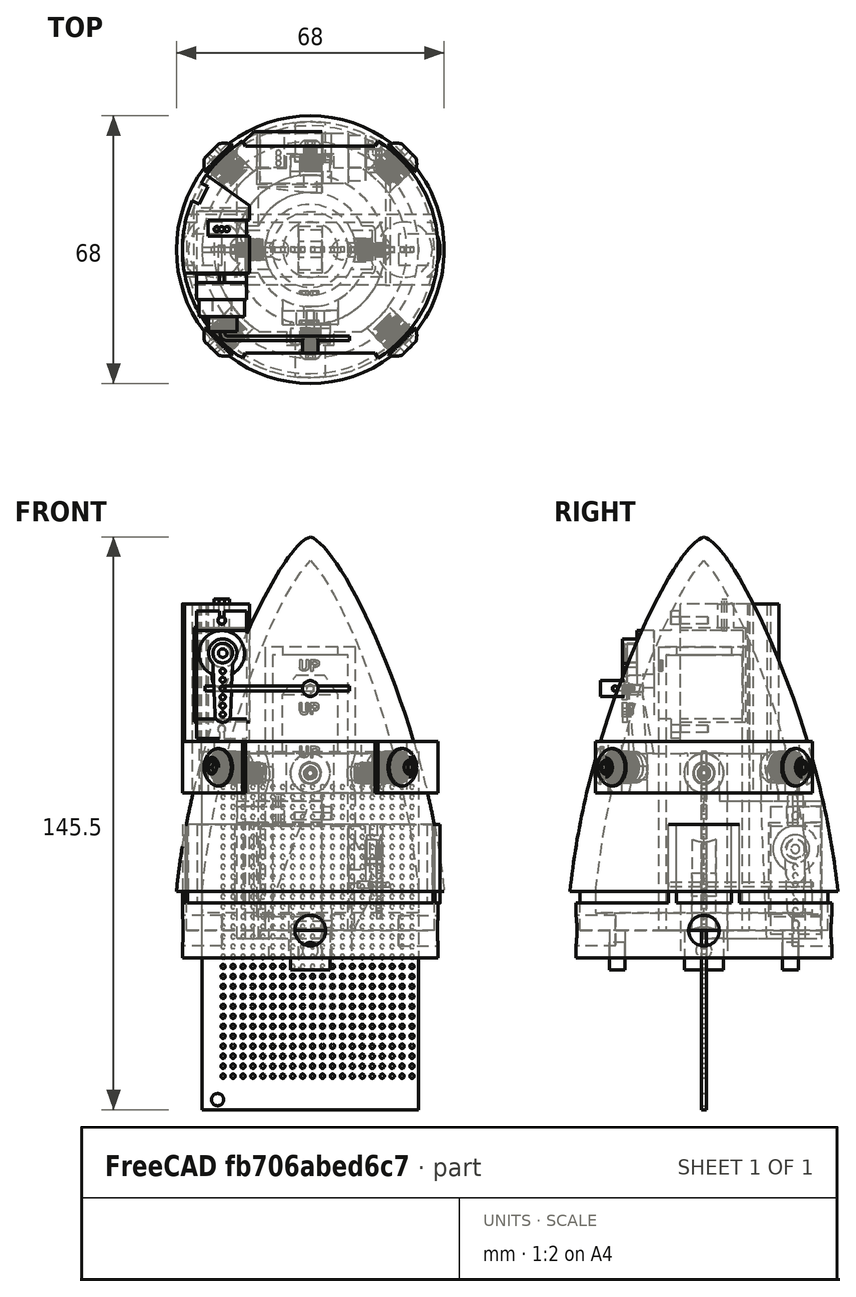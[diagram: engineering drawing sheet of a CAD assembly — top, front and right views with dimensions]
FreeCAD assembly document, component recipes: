
FREECAD ASSEMBLY — COMPONENT RECIPES ("slider")

This assembly document has 5 components, labeled P0..P4 below (a component is one placed body or linked part). 4 of them carry a construction recipe — the FreeCAD feature program that regenerates the part from scratch, quoted from this document or its linked companion documents; the rest are supplied as boundary geometry only. No exploded tour is included for this assembly.
COMPONENT P0 — recipe-attached ("66mm x 18" Body Tube", modeled in this document).
Construction recipe (the document's own serialized feature program — sketch geometry with constraints, then the solid features built on it; lengths are millimeters unless a unit is written):

FEATURE [Sketcher::SketchObject] Sketch006  label="Body Tube Sketch"
  FullyConstrained = true
  MapMode = 5
  Support = -> [XY_Plane004]
  sketch-geometry (2):
    g0: Circle CenterX=0 CenterY=0 CenterZ=0 NormalX=0 NormalY=0 NormalZ=1 AngleXU=0 Radius=33
    g1: Circle CenterX=0 CenterY=0 CenterZ=0 NormalX=0 NormalY=0 NormalZ=1 AngleXU=0 Radius=32.5
  constraints (4):
    c: Diameter(g0) = 66  'Outer Diameter'
    c: Diameter(g1) = 65  'Inner Diameter'
    c: Coincident(g1,g-1)  'Center1'
    c: Coincident(g1,g0)  'Center2'
FEATURE [PartDesign::Pad] Pad002  label="Body Tube Pad"
  AllowMultiFace = false
  Direction = (1,1,1)
  Length = 457.2
  Length2 = 100
  Profile = -> Sketch006
  Type = 0
FEATURE [Sketcher::SketchObject] Sketch  label="Exhaust Vent"
  FullyConstrained = false
  MapMode = 5
  Placement = pos=(0,0,0) rot=(1,0,0;1.5708rad)
  Support = -> [XZ_Plane004]
  sketch-geometry (4):
    g0: LineSegment StartX=-9 StartY=98 StartZ=0 EndX=9 EndY=98 EndZ=0
    g1: LineSegment StartX=9 StartY=98 StartZ=0 EndX=9 EndY=80 EndZ=0
    g2: LineSegment StartX=9 StartY=80 StartZ=0 EndX=-9 EndY=80 EndZ=0
    g3: LineSegment StartX=-9 StartY=80 StartZ=0 EndX=-9 EndY=98 EndZ=0
  constraints (14):
    c: Coincident(g0,g1)
    c: Coincident(g1,g2)
    c: Coincident(g2,g3)
    c: Coincident(g3,g0)
    c: Horizontal(g0)
    c: Horizontal(g2)
    c: Vertical(g1)
    c: Vertical(g3)
    c: DistanceX(g2,g2) = 18
    c: Distance(g-1,g2) = 80
    c: Equal(g0,g3)
    c: Equal(g3,g2)
    c: Equal(g2,g1)
    c: DistanceX(g2,g-1) = 9
FEATURE [PartDesign::Pocket] Pocket
  AllowMultiFace = false
  BaseFeature = -> Pad002
  Length = 5
  Length2 = 100
  Midplane = true
  Profile = -> Sketch
  Type = 1
FEATURE [Sketcher::SketchObject] Sketch022  label="M5 Parachute Mounting Holes"
  FullyConstrained = false
  MapMode = 5
  Placement = pos=(0,0,0) rot=(1,0,0;1.5708rad)
  Support = -> [XZ_Plane004]
  sketch-geometry (1):
    g0: Circle CenterX=0 CenterY=418 CenterZ=0 NormalX=0 NormalY=0 NormalZ=1 AngleXU=0 Radius=2.4
  constraints (3):
    c: Diameter(g0) = 4.8
    c: PointOnObject(g0,g-2)
    c: DistanceY(g0) = 418
FEATURE [PartDesign::Pocket] Pocket010
  AllowMultiFace = false
  BaseFeature = -> Pocket
  Length = 5
  Length2 = 100
  Profile = -> Sketch022
  Type = 1
FEATURE [PartDesign::PolarPattern] PolarPattern001
  Angle = 360
  Axis = -> Sketch022 [V_Axis]
  BaseFeature = -> Pocket010
  Occurrences = 4
  Originals = -> [Pocket010]
FEATURE [Sketcher::SketchObject] Sketch056  label="[Body Tube] Middle Motor Gimbal Servo Cutout"
  AttachmentOffset = pos=(0,0,-33) rot=(0,1,0;3.14159rad)
  FullyConstrained = false
  MapMode = 5
  Placement = pos=(0,33,7.3e-15) rot=(0,0.707107,0.707107;3.14159rad)
  Support = -> [XZ_Plane004]
  sketch-geometry (4):
    g0: LineSegment StartX=8 StartY=46 StartZ=0 EndX=23 EndY=46 EndZ=0
    g1: LineSegment StartX=23 StartY=46 StartZ=0 EndX=23 EndY=8 EndZ=0
    g2: LineSegment StartX=23 StartY=8 StartZ=0 EndX=8 EndY=8 EndZ=0
    g3: LineSegment StartX=8 StartY=8 StartZ=0 EndX=8 EndY=46 EndZ=0
  constraints (12):
    c: Coincident(g0,g1)
    c: Coincident(g1,g2)
    c: Coincident(g2,g3)
    c: Coincident(g3,g0)
    c: Horizontal(g0)
    c: Horizontal(g2)
    c: Vertical(g1)
    c: Vertical(g3)
    c: DistanceY(g3,g3) = 38
    c: DistanceX(g0,g0) = 15
    c: DistanceX(g2) = 8
    c: DistanceY(g2) = 8
FEATURE [PartDesign::Pocket] Pocket026
  BaseFeature = -> PolarPattern001
  Length = 15
  Length2 = 100
  Profile = -> Sketch056
  Type = 0
FEATURE [Sketcher::SketchObject] Sketch085  label="[Body Tube] Outer Motor Gimbal Servo Cutout"
  FullyConstrained = false
  MapMode = 5
  Placement = pos=(0,0,0) rot=(0.57735,0.57735,0.57735;2.0944rad)
  Support = -> [YZ_Plane004]
  sketch-geometry (4):
    g0: LineSegment StartX=-13 StartY=88 StartZ=0 EndX=-25 EndY=88 EndZ=0
    g1: LineSegment StartX=-25 StartY=88 StartZ=0 EndX=-25 EndY=60 EndZ=0
    g2: LineSegment StartX=-25 StartY=60 StartZ=0 EndX=-13 EndY=60 EndZ=0
    g3: LineSegment StartX=-13 StartY=60 StartZ=0 EndX=-13 EndY=88 EndZ=0
  constraints (12):
    c: Coincident(g0,g1)
    c: Coincident(g1,g2)
    c: Coincident(g2,g3)
    c: Coincident(g3,g0)
    c: Horizontal(g0)
    c: Horizontal(g2)
    c: Vertical(g1)
    c: Vertical(g3)
    c: DistanceX(g2) = -13
    c: DistanceY(g2) = 60
    c: DistanceX(g0,g0) = 12
    c: DistanceY(g1,g1) = 28
FEATURE [PartDesign::Pocket] Pocket044
  BaseFeature = -> Pocket026
  Length = 5
  Length2 = 100
  Profile = -> Sketch085
  Type = 1
FEATURE [PartDesign::Body] Body004  label="66mm x 18" Body Tube"
  Group = -> [Sketch006,Pad002,Sketch,Pocket,Sketch022,Pocket010,PolarPattern001,Sketch056,Pocket026,Sketch085,Pocket044]
  Origin = -> Origin005
  Tip = -> Pocket044
COMPONENT P1 — recipe-attached ("Nose Cone Assembly", modeled in this document).
Construction recipe (the document's own serialized feature program — sketch geometry with constraints, then the solid features built on it; lengths are millimeters unless a unit is written):

FEATURE [Sketcher::SketchObject] Sketch007  label="[Nose Cone] Nose Cone Shape"
  FullyConstrained = false
  MapMode = 5
  Placement = pos=(0,0,0) rot=(1,0,0;1.5708rad)
  Support = -> [XZ_Plane005]
  sketch-geometry (21):
    g0: LineSegment StartX=0 StartY=0 StartZ=0 EndX=31.5 EndY=0 EndZ=0
    g1: LineSegment StartX=31.5 StartY=0 StartZ=0 EndX=31.5 EndY=10 EndZ=0
    g2: LineSegment StartX=31.5 StartY=10 StartZ=0 EndX=34 EndY=10 EndZ=0
    g3: LineSegment StartX=0 StartY=0 StartZ=0 EndX=0 EndY=4.5 EndZ=0
    g4: LineSegment StartX=0 StartY=4.5 StartZ=0 EndX=27.5 EndY=4.5 EndZ=0
    g5: LineSegment StartX=0 StartY=100 StartZ=0 EndX=0 EndY=94 EndZ=0
    g6-g9: Circle x4 (B-spline internal-alignment scaffolding for g10; pole/knot coordinates omitted)
    g10: BSplineCurve PolesCount=4 KnotsCount=2 Degree=3 IsPeriodic=0
    g11: GeomPoint X=0 Y=100 Z=0
    g12: GeomPoint X=34 Y=10 Z=0
    g13-g16: Circle x4 (B-spline internal-alignment scaffolding for g17; pole/knot coordinates omitted)
    g17: BSplineCurve PolesCount=4 KnotsCount=2 Degree=3 IsPeriodic=0
    g18: GeomPoint X=0 Y=94 Z=0
    g19: GeomPoint X=27.5 Y=10 Z=0
    g20: LineSegment StartX=27.5 StartY=10 StartZ=0 EndX=27.5 EndY=4.5 EndZ=0
  constraints (48):
    c: Coincident(g0,g-1)
    c: Horizontal(g0)
    c: Coincident(g1,g0)
    c: Vertical(g1)
    c: Coincident(g2,g1)
    c: Horizontal(g2)
    c: DistanceX(g0,g0) = 31.5
    c: DistanceX(g0,g2) = 34
    c: DistanceY(g0,g5) = 100
    c: DistanceY(g1,g1) = 10
    c: PointOnObject(g5,g-2)
    c: Coincident(g3,g0)
    c: PointOnObject(g3,g-2)
    c: Coincident(g4,g3)
    c: Horizontal(g4)
    c: Vertical(g5)
    c: DistanceY(g5,g5) = 6
    c: DistanceX(g4,g2) = 6.5
    c: Coincident(g10,g5)
    c: Weight(g6) = 1
    c: Equal(g6,g7)
    c: Equal(g6,g8)
    c: Equal(g6,g9)
    c: Coincident(g10,g2)
    c: InternalAlignment(g6-g9 -> g10) x4
    c: InternalAlignment(g11,g10)
    c: InternalAlignment(g12,g10)
    c: DistanceY(g7,g5) = 2
    c: DistanceX(g5,g7) = 8
    c: DistanceY(g2,g8) = 42
    c: DistanceX(g8,g2) = 4
    c: Coincident(g17,g5)
    c: Weight(g13) = 1
    c: Equal(g13,g14)
    c: Equal(g13,g15)
    c: Equal(g13,g16)
    c: InternalAlignment(g13-g16 -> g17) x4
    c: InternalAlignment(g18,g17)
    c: InternalAlignment(g19,g17)
    c: DistanceX(g14,g7) = 0
    c: DistanceY(g8,g15) = 0
    c: DistanceX(g15,g8) = 7
    c: DistanceY(g14,g7) = 12
    c: DistanceY(g0,g3) = 4.5
    c: Coincident(g20,g17)
    c: Coincident(g20,g4)
    c: Vertical(g20)
    c: DistanceY(g1,g17) = 0
FEATURE [Sketcher::SketchObject] Sketch020  label="[Nose Cone] Parachute and Shock Cord Mount"
  FullyConstrained = false
  MapMode = 5
  Placement = pos=(0,0,0) rot=(1,0,0;3.14159rad)
  sketch-geometry (8):
    g0: LineSegment StartX=-5 StartY=24 StartZ=0 EndX=5 EndY=24 EndZ=0
    g1: LineSegment StartX=5 StartY=24 StartZ=0 EndX=5 EndY=20 EndZ=0
    g2: LineSegment StartX=5 StartY=20 StartZ=0 EndX=-5 EndY=20 EndZ=0
    g3: LineSegment StartX=-5 StartY=20 StartZ=0 EndX=-5 EndY=24 EndZ=0
    g4: LineSegment StartX=-5 StartY=-20 StartZ=0 EndX=5 EndY=-20 EndZ=0
    g5: LineSegment StartX=5 StartY=-20 StartZ=0 EndX=5 EndY=-24 EndZ=0
    g6: LineSegment StartX=5 StartY=-24 StartZ=0 EndX=-5 EndY=-24 EndZ=0
    g7: LineSegment StartX=-5 StartY=-24 StartZ=0 EndX=-5 EndY=-20 EndZ=0
  constraints (22):
    c: Coincident(g0,g1)
    c: Coincident(g1,g2)
    c: Coincident(g2,g3)
    c: Coincident(g3,g0)
    c: Vertical(g1)
    c: Coincident(g4,g5)
    c: Coincident(g5,g6)
    c: Coincident(g6,g7)
    c: Coincident(g7,g4)
    c: Horizontal(g4)
    c: Vertical(g5)
    c: Equal(g7,g5)
    c: Equal(g5,g3)
    c: Equal(g3,g1)
    c: Equal(g0,g2)
    c: Equal(g2,g4)
    c: Equal(g4,g6)
    c: Symmetric(g2,g4,g-1)
    c: DistanceX(g2,g2) = 10
    c: DistanceY(g1,g1) = 4
    c: DistanceY(g2) = 20
    c: Symmetric(g2,g1,g-2)
FEATURE [PartDesign::Revolution] Revolution001  label="Revolution"
  AllowMultiFace = false
  Angle = 360
  Axis = (-3e-16,3e-16,1)
  Base = (0,0,0)
  Placement = pos=(0,0,0) rot=(1,0,0;1.5708rad)
  Profile = -> Sketch007
  ReferenceAxis = -> Z_Axis005
FEATURE [PartDesign::Pad] Pad006
  AllowMultiFace = false
  BaseFeature = -> Revolution001
  Direction = (1,1,1)
  Length = 10
  Length2 = 100
  Placement = pos=(0,0,0) rot=(1,0,0;1.5708rad)
  Profile = -> Sketch020
  Type = 0
FEATURE [Sketcher::SketchObject] Sketch021  label="[Nose Cone] Parachute and Shock Cord Hole"
  FullyConstrained = false
  MapMode = 5
  Placement = pos=(0,-24,5.3e-15) rot=(1,0,0;1.5708rad)
  Support = -> [Pad006]
  sketch-geometry (1):
    g0: Circle CenterX=0 CenterY=-5 CenterZ=0 NormalX=0 NormalY=0 NormalZ=1 AngleXU=0 Radius=2
  constraints (3):
    c: DistanceY(g0,g-1) = 5
    c: Diameter(g0) = 4
    c: PointOnObject(g0,g-2)
FEATURE [PartDesign::Pocket] Pocket007
  AllowMultiFace = false
  BaseFeature = -> Pad006
  Length = 5
  Length2 = 100
  Placement = pos=(0,0,0) rot=(1,0,0;1.5708rad)
  Profile = -> Sketch021
  Type = 1
FEATURE [Sketcher::SketchObject] Sketch026  label="[Nose Cone] Hold Down Mount"
  FullyConstrained = false
  MapMode = 5
  Placement = pos=(0,0,0) rot=(1,0,0;3.14159rad)
  Support = -> [Pocket007]
  sketch-geometry (4):
    g0: LineSegment StartX=-3 StartY=5 StartZ=0 EndX=3 EndY=5 EndZ=0
    g1: LineSegment StartX=3 StartY=5 StartZ=0 EndX=3 EndY=-5 EndZ=0
    g2: LineSegment StartX=3 StartY=-5 StartZ=0 EndX=-3 EndY=-5 EndZ=0
    g3: LineSegment StartX=-3 StartY=-5 StartZ=0 EndX=-3 EndY=5 EndZ=0
  constraints (11):
    c: Coincident(g0,g1)
    c: Coincident(g1,g2)
    c: Coincident(g2,g3)
    c: Coincident(g3,g0)
    c: Horizontal(g0)
    c: Horizontal(g2)
    c: Vertical(g1)
    c: Vertical(g3)
    c: Symmetric(g0,g1,g-1)
    c: DistanceY(g3,g3) = 10
    c: DistanceX(g0,g0) = 6
FEATURE [PartDesign::Pad] Pad010
  AllowMultiFace = false
  BaseFeature = -> Pocket007
  Direction = (1,1,1)
  Length = 10
  Length2 = 100
  Placement = pos=(0,0,0) rot=(1,0,0;1.5708rad)
  Profile = -> Sketch026
  Type = 0
FEATURE [Sketcher::SketchObject] Sketch027  label="[Nose Cone] Hold Down Hole"
  FullyConstrained = false
  MapMode = 5
  Placement = pos=(-3,0,-1e-15) rot=(0.707107,0,-0.707107;3.14159rad)
  Support = -> [Pad010]
  sketch-geometry (1):
    g0: Circle CenterX=5 CenterY=0 CenterZ=0 NormalX=0 NormalY=0 NormalZ=1 AngleXU=0 Radius=2
  constraints (3):
    c: PointOnObject(g0,g-1)
    c: Diameter(g0) = 4
    c: DistanceX(g-1,g0) = 5
FEATURE [PartDesign::Pocket] Pocket015
  AllowMultiFace = false
  BaseFeature = -> Pad010
  Length = 5
  Length2 = 100
  Placement = pos=(0,0,0) rot=(1,0,0;1.5708rad)
  Profile = -> Sketch027
  Type = 1
FEATURE [PartDesign::Body] Body003  label="Nose Cone"
  Group = -> [Sketch007,Revolution001,Sketch020,Pad006,Sketch021,Pocket007,Sketch026,Pad010,Sketch027,Pocket015]
  Origin = -> Origin004
  Tip = -> Pocket015
COMPONENT P2 — recipe-attached ("Parachute Deployment", modeled in this document).
Construction recipe (the document's own serialized feature program — sketch geometry with constraints, then the solid features built on it; lengths are millimeters unless a unit is written):

FEATURE [Sketcher::SketchObject] Sketch009  label="[Parachute Holding] Base"
  FullyConstrained = false
  MapMode = 5
  Support = -> [XY_Plane007]
  sketch-geometry (1):
    g0: Circle CenterX=0 CenterY=0 CenterZ=0 NormalX=0 NormalY=0 NormalZ=1 AngleXU=0 Radius=32.5
  constraints (2):
    c: Coincident(g0,g-1)
    c: Diameter(g0) = 65
FEATURE [PartDesign::Pad] Pad
  AllowMultiFace = false
  Direction = (1,1,1)
  Length = 14
  Length2 = 100
  Midplane = true
  Profile = -> Sketch009
  Type = 0
FEATURE [Sketcher::SketchObject] Sketch011  label="M5 Insert Sketch"
  FullyConstrained = false
  MapMode = 5
  Placement = pos=(0,32.5,0) rot=(0,0.707107,0.707107;3.14159rad)
  sketch-geometry (1):
    g0: Circle CenterX=0 CenterY=0 CenterZ=0 NormalX=0 NormalY=0 NormalZ=1 AngleXU=0 Radius=3.9
  constraints (2):
    c: Coincident(g0,g-1)
    c: Diameter(g0) = 7.8
FEATURE [PartDesign::Pocket] Pocket001
  AllowMultiFace = false
  BaseFeature = -> Pad
  Length = 10.05
  Length2 = 100
  Profile = -> Sketch011
  Type = 0
FEATURE [PartDesign::PolarPattern] PolarPattern
  Angle = 360
  Axis = -> Z_Axis007
  BaseFeature = -> Pocket001
  Occurrences = 4
  Originals = -> [Pocket001]
FEATURE [Sketcher::SketchObject] Sketch012  label="[Parachute Holding] Parachute Seperator"
  FullyConstrained = false
  MapMode = 5
  Placement = pos=(0,0,7) rot=(0,0,1;0rad)
  Support = -> [PolarPattern]
  sketch-geometry (4):
    g0: LineSegment StartX=31.7372 StartY=-7 StartZ=0 EndX=-31.7372 EndY=-7 EndZ=0
    g1: LineSegment StartX=31.229 StartY=-9 StartZ=0 EndX=-31.229 EndY=-9 EndZ=0
    g2: ArcOfCircle CenterX=0 CenterY=0 CenterZ=0 NormalX=0 NormalY=0 NormalZ=1 AngleXU=0 Radius=32.5 StartAngle=3.35868 EndAngle=3.42218
    g3: ArcOfCircle CenterX=0 CenterY=0 CenterZ=0 NormalX=0 NormalY=0 NormalZ=1 AngleXU=0 Radius=32.5 StartAngle=6.00259 EndAngle=6.0661
  constraints (11):
    c: Symmetric(g0,g0,g-2)
    c: Symmetric(g1,g1,g-2)
    c: DistanceY(g1,g-1) = 9
    c: DistanceY(g1,g0) = 2
    c: Coincident(g2,g-1)
    c: Coincident(g2,g1)
    c: Coincident(g2,g0)
    c: Coincident(g3,g2)
    c: Coincident(g3,g1)
    c: Coincident(g3,g0)
    c: Distance(g0,g2) = 32.5
FEATURE [PartDesign::Pad] Pad004
  AllowMultiFace = false
  BaseFeature = -> PolarPattern
  Direction = (1,1,1)
  Length = 20
  Length2 = 100
  Profile = -> Sketch012
  Type = 0
FEATURE [Sketcher::SketchObject] Sketch013  label="[Parachute Holding] Nose Cone Hold Down Holes"
  FullyConstrained = false
  MapMode = 5
  Placement = pos=(0,0,7) rot=(0,0,1;0rad)
  sketch-geometry (6):
    g0: Circle CenterX=-8 CenterY=0 CenterZ=0 NormalX=0 NormalY=0 NormalZ=1 AngleXU=0 Radius=2.5
    g1: Circle CenterX=8 CenterY=0 CenterZ=0 NormalX=0 NormalY=0 NormalZ=1 AngleXU=0 Radius=2.5
    g2: LineSegment StartX=-3 StartY=6 StartZ=0 EndX=3 EndY=6 EndZ=0
    g3: LineSegment StartX=3 StartY=6 StartZ=0 EndX=3 EndY=-6 EndZ=0
    g4: LineSegment StartX=3 StartY=-6 StartZ=0 EndX=-3 EndY=-6 EndZ=0
    g5: LineSegment StartX=-3 StartY=-6 StartZ=0 EndX=-3 EndY=6 EndZ=0
  constraints (16):
    c: PointOnObject(g0,g-1)
    c: Symmetric(g0,g1,g-2)
    c: Diameter(g0) = 5
    c: Diameter(g1) = 5
    c: Distance(g-1,g0) = 8
    c: Coincident(g2,g3)
    c: Coincident(g3,g4)
    c: Coincident(g4,g5)
    c: Coincident(g5,g2)
    c: Horizontal(g2)
    c: Horizontal(g4)
    c: Vertical(g3)
    c: Vertical(g5)
    c: Symmetric(g3,g2,g-1)
    c: DistanceX(g4,g4) = 6
    c: DistanceY(g3,g3) = 12
FEATURE [Sketcher::SketchObject] Sketch015  label="[Parachute Holding] Spring Mounts"
  FullyConstrained = false
  MapMode = 5
  Placement = pos=(0,0,7) rot=(0,0,1;0rad)
  sketch-geometry (4):
    g0: Circle CenterX=24 CenterY=0 CenterZ=0 NormalX=0 NormalY=0 NormalZ=1 AngleXU=0 Radius=9
    g1: Circle CenterX=-24 CenterY=0 CenterZ=0 NormalX=0 NormalY=0 NormalZ=1 AngleXU=0 Radius=8.5
    g2: Circle CenterX=24 CenterY=0 CenterZ=0 NormalX=0 NormalY=0 NormalZ=1 AngleXU=0 Radius=7
    g3: Circle CenterX=-24 CenterY=0 CenterZ=0 NormalX=0 NormalY=0 NormalZ=1 AngleXU=0 Radius=7
  constraints (9):
    c: Diameter(g0) = 18
    c: Diameter(g1) = 17
    c: Coincident(g2,g0)
    c: Diameter(g2) = 14
    c: Coincident(g3,g1)
    c: Diameter(g3) = 14
    c: Symmetric(g0,g1,g-1)
    c: PointOnObject(g0,g-1)
    c: DistanceX(g-1,g0) = 24
FEATURE [PartDesign::PolarPattern] PolarPattern002
  Angle = 360
  Axis = -> Sketch012 [N_Axis]
  BaseFeature = -> Pad004
  Occurrences = 2
  Originals = -> [Pad004]
FEATURE [PartDesign::Pocket] Pocket014
  AllowMultiFace = false
  BaseFeature = -> PolarPattern002
  Length = 5
  Length2 = 100
  Profile = -> Sketch013
  Type = 1
FEATURE [PartDesign::Pad] Pad009
  AllowMultiFace = false
  BaseFeature = -> Pocket014
  Direction = (1,1,1)
  Length = 20
  Length2 = 100
  Profile = -> Sketch015
  Type = 0
FEATURE [PartDesign::Body] Body006  label="Parachute Holding"
  Group = -> [Sketch009,Pad,Sketch011,Pocket001,PolarPattern,Sketch012,Pad004,Sketch013,Sketch015,PolarPattern002,Pocket014,Pad009]
  Origin = -> Origin007
  Tip = -> Pad009
COMPONENT P3 — recipe-attached ("Motor Mount", modeled in this document).
Construction recipe (the document's own serialized feature program — sketch geometry with constraints, then the solid features built on it; lengths are millimeters unless a unit is written):

FEATURE [Sketcher::SketchObject] Sketch008  label="Motor Tube Sketch"
  FullyConstrained = false
  MapMode = 5
  Support = -> [XY_Plane006]
  sketch-geometry (2):
    g0: Circle CenterX=0 CenterY=0 CenterZ=0 NormalX=0 NormalY=0 NormalZ=1 AngleXU=0 Radius=9
    g1: Circle CenterX=0 CenterY=0 CenterZ=0 NormalX=0 NormalY=0 NormalZ=1 AngleXU=0 Radius=9.35
  constraints (4):
    c: Coincident(g0,g-1)
    c: Coincident(g1,g0)
    c: Diameter(g0) = 18
    c: Diameter(g1) = 18.7
FEATURE [PartDesign::Pad] Pad003  label="Motor Tube Pad"
  AllowMultiFace = false
  Direction = (1,1,1)
  Length = 69.9
  Length2 = 100
  Profile = -> Sketch008
  Type = 0
FEATURE [PartDesign::Body] Body005  label="18mm x 2.75" Motor Tube"
  Group = -> [Sketch008,Pad003]
  Origin = -> Origin006
  Tip = -> Pad003
FEATURE [Sketcher::SketchObject] Sketch038
  FullyConstrained = false
  MapMode = 5
  Support = -> [XY_Plane013]
  sketch-geometry (1):
    g0: Circle CenterX=0 CenterY=0 CenterZ=0 NormalX=0 NormalY=0 NormalZ=1 AngleXU=0 Radius=8.75
  constraints (2):
    c: Coincident(g0,g-1)
    c: Diameter(g0) = 17.5
FEATURE [PartDesign::Pad] Pad019
  Direction = (1,1,1)
  Length = 69.5
  Length2 = 100
  Profile = -> Sketch038
  Type = 0
FEATURE [PartDesign::Body] Body009  label="Estes A-C Motor"
  Group = -> [Sketch038,Pad019]
  Origin = -> Origin013
  Tip = -> Pad019
COMPONENT P4 — geometry summary ("Avionics"; no construction recipe available for this part):
  bounding box: 91.0 x 55.0 x 1.3 mm
  tessellated surface: 48,444 triangles
  volume: 7666 mm^3 (118% of its bounding box)
  symmetry: 2-fold rotationally symmetric about the x axis; 2-fold rotationally symmetric about the y axis; 2-fold rotationally symmetric about the z axis; mirror-symmetric across its x mid-plane, y mid-plane, z mid-plane
PROVENANCE & LICENSES
A FreeCAD (.FCStd) document from a public repository crawl; recipes are the document's own serialized feature recipes (and, for linked parts, companion documents' recipes).
License: gpl-3.0.
